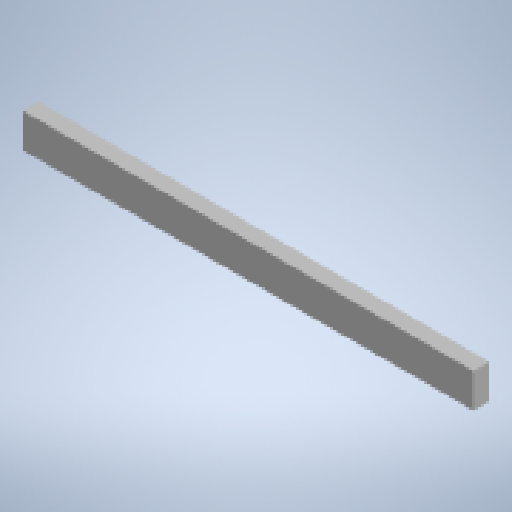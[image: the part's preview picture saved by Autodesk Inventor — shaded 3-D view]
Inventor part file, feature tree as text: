
AUTODESK INVENTOR PART (.ipt)
format: ipt  version: 2023 (Build 270158000, 158)  size: 129,536 bytes
history: native  units: in
note: dims shown in document units (in); Inventor stores cm internally (conversion verified against a paired STEP export)
features: extrude x1, sketch x1
ambient origin geometry x8: Origin, YZ Plane, XZ Plane, XY Plane, X Axis, Y Axis, Z Axis, Center Point
bodies: Solid1 (feature_tree)
feature tree (2):
  extrude  "Extrusion1"  Depth=3.75in
  sketch  "Sketch1"  dims[d0=1.75in d1=3.75in d2=49.5in d3=0.0in]
